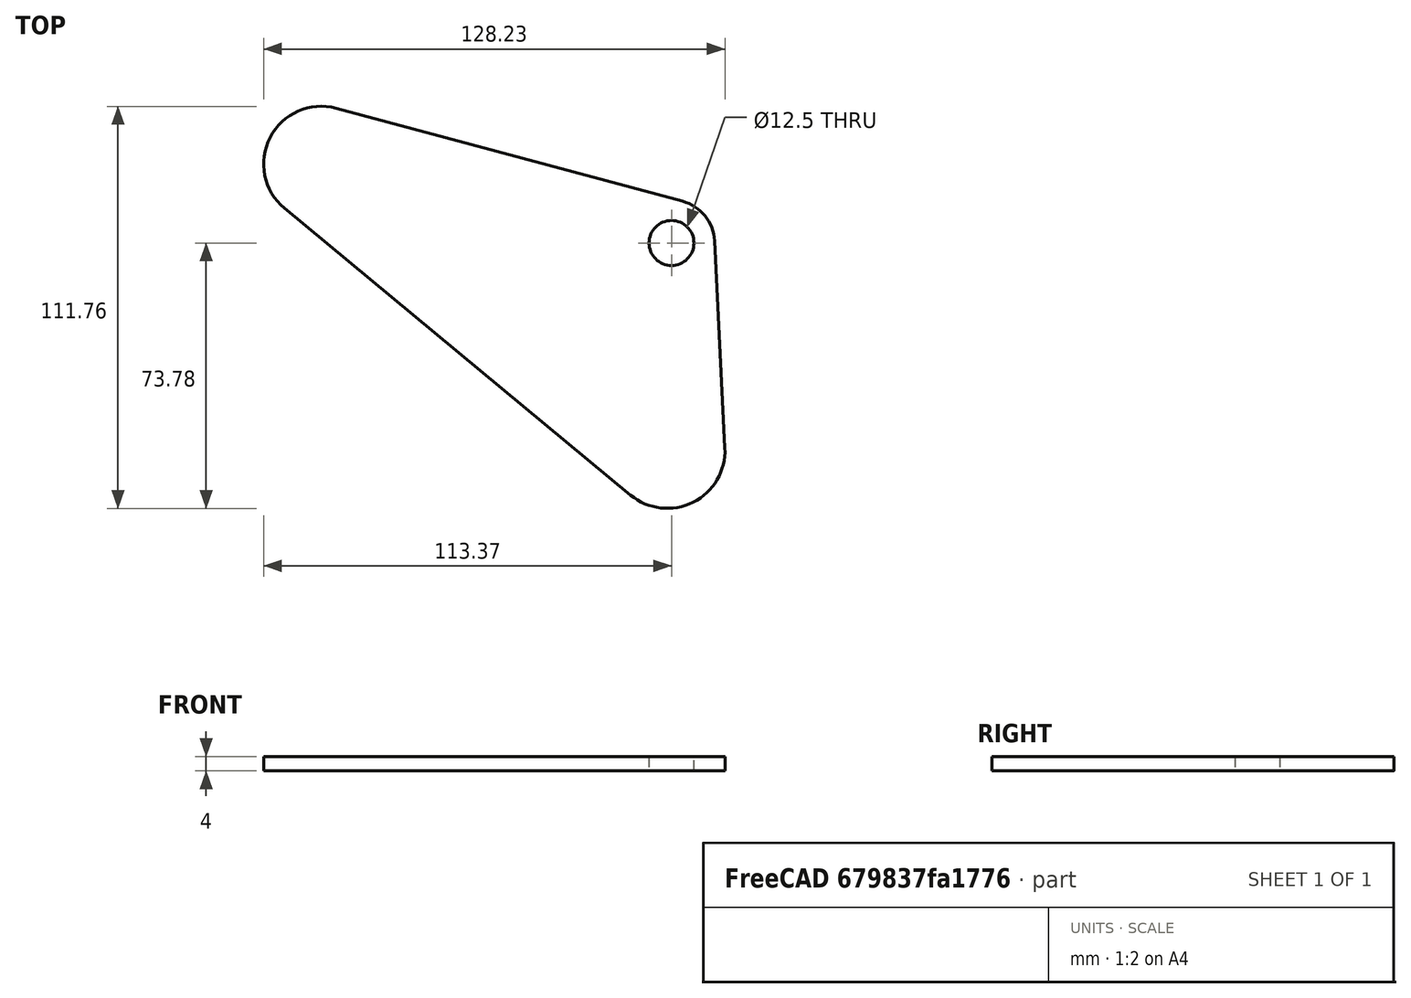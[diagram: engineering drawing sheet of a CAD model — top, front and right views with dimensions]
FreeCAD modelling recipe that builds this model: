
FCSTD DOCUMENT  (FreeCAD 0.19R24267 +99 (Git))
Label: V2 Range pin retainer plate all pin locations
License: All rights reserved
LicenseURL: http://en.wikipedia.org/wiki/All_rights_reserved
objects: Sketcher::SketchObject×1, PartDesign::Pad×1, PartDesign::Body×1
note: 4 computed .brp shape members not serialized (recipe doc carries the construction recipe); baked Part::Feature solids carry a one-line shape summary decoded from their .brp

FEATURE [Sketcher::SketchObject] Sketch
  FullyConstrained = true
  MapMode = 5
  Support = -> [XY_Plane]
  sketch-geometry (7):
    g0: Circle CenterX=0 CenterY=0 CenterZ=0 NormalX=0 NormalY=0 NormalZ=1 AngleXU=0 Radius=6.25
    g1: ArcOfCircle CenterX=-97.37 CenterY=21.98 CenterZ=0 NormalX=0 NormalY=0 NormalZ=1 AngleXU=0 Radius=16 StartAngle=1.3087 EndAngle=4.0203
    g2: ArcOfCircle CenterX=-1.14 CenterY=-57.78 CenterZ=0 NormalX=0 NormalY=0 NormalZ=1 AngleXU=0 Radius=16 StartAngle=4.0203 EndAngle=6.33273
    g3: LineSegment StartX=-107.58 StartY=9.66133 StartZ=0 EndX=-11.3503 EndY=-70.0987 EndZ=0
    g4: ArcOfCircle CenterX=0 CenterY=0 CenterZ=0 NormalX=0 NormalY=0 NormalZ=1 AngleXU=0 Radius=12 StartAngle=0.0495426 EndAngle=1.3087
    g5: LineSegment StartX=-93.2243 StartY=37.4336 StartZ=0 EndX=3.1093 EndY=11.5902 EndZ=0
    g6: LineSegment StartX=11.9853 StartY=0.594268 StartZ=0 EndX=14.8404 EndY=-56.9876 EndZ=0
  constraints (16):
    c: Coincident(g0,g-1)
    c: DistanceX(g1,g0) = 97.37
    c: DistanceX(g2,g0) = 1.14
    c: DistanceY(g0,g1) = 21.98
    c: DistanceY(g2,g0) = 57.78
    c: Equal(g1,g2)
    c: Diameter(g1) = 32
    c: Coincident(g4,g0)
    c: Diameter(g4) = 24
    c: Tangent(g1,g5) = 1.5708
    c: Tangent(g2,g3) = -1.5708
    c: Tangent(g1,g3) = -1.5708
    c: Tangent(g2,g6) = 1.5708
    c: Tangent(g4,g6) = 1.5708
    c: Tangent(g4,g5) = 1.5708
    c: Diameter(g0) = 12.5
FEATURE [PartDesign::Pad] Pad
  Direction = (1,1,1)
  Length = 4
  Length2 = 100
  Profile = -> Sketch
  Type = 0
FEATURE [PartDesign::Body] Body
  Group = -> [Sketch,Pad]
  Origin = -> Origin
  Tip = -> Pad
